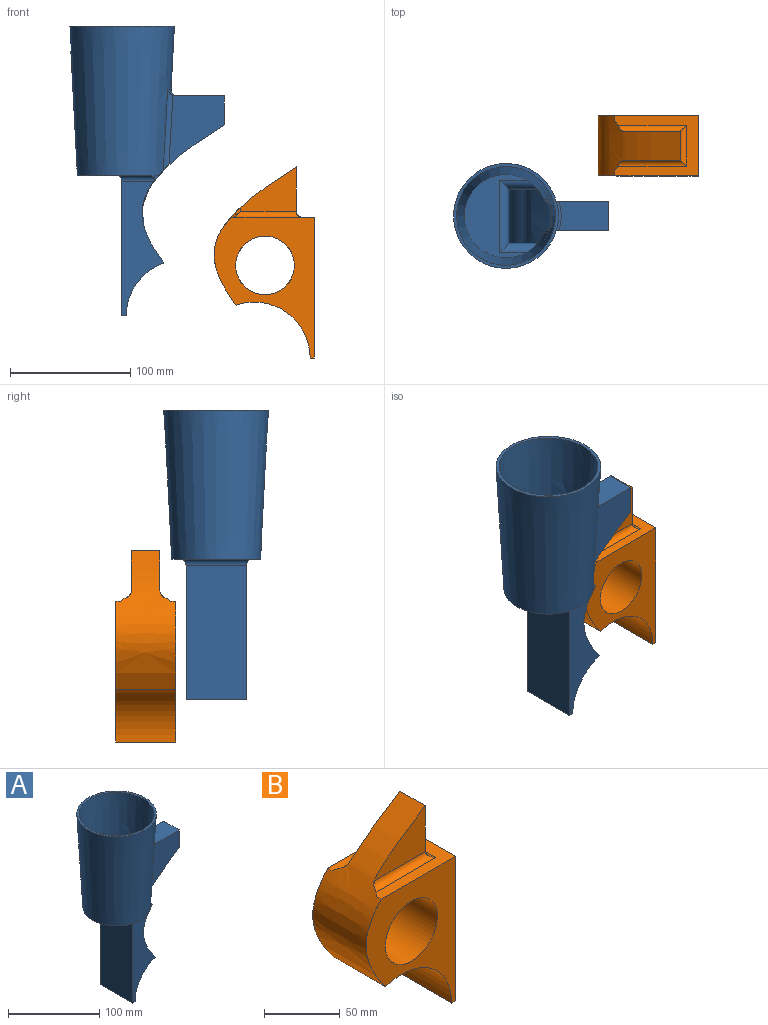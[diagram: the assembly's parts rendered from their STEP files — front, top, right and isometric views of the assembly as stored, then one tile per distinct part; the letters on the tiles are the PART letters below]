
ASSEMBLY  parts=2 mates=1
PART A: 40 faces, bbox 130.1x88.3x242.1 mm
  f0: plane 4.11x3.25mm, normal (0,0,1), area 6.4mm2, adj f2,f6,f22
  f1: plane 4.11x3.25mm, normal (0,0,1), area 6.4mm2, adj f2,f4,f22
  f2: cone r=37.09mm half-angle=3deg, axis (0,0,1), area 29261.2mm2, adj f0,f1,f4,f6,f11,f12,f13,f14
  f3: plane 113.11x35.98mm, normal (0,1,0), area 2016.9mm2, adj f10,f13,f15,f16,f22
  f4: plane 4.33x3.57mm, normal (0,1,0), area 6.8mm2, adj f1,f2,f22
  f5: plane 113.11x35.98mm, normal (0,-1,0), area 2016.9mm2, adj f10,f14,f15,f16,f22
  f6: plane 4.33x3.57mm, normal (0,-1,0), area 6.8mm2, adj f0,f2,f22
  f7: plane 58.25x46.77mm, normal (0,-1,0), area 1734.9mm2, adj f9,f12,f19,f20,f22
  f8: plane 58.25x46.77mm, normal (0,1,0), area 1734.9mm2, adj f9,f11,f19,f20,f22
  f9: plane 24.06x23.84mm, normal (1,0,0), area 573.7mm2, adj f7,f8,f19,f22
  f10: cylinder r=46.49mm len=50mm, axis (0,1,0), area 2880.8mm2, adj f3,f5,f15,f22
  f11: bspline ~111.12x10.85mm, area 369.3mm2, adj f2,f8,f20,f22
  f12: bspline ~111.12x10.85mm, area 369.3mm2, adj f2,f7,f20,f22
  f13: cylinder r=5mm len=32.05mm, axis (1,0,0), area 213.5mm2, adj f2,f3,f17,f21,f22
  f14: cylinder r=5mm len=32.05mm, axis (-1,0,0), area 213.5mm2, adj f2,f5,f17,f21,f22
  f15: plane 50x3.51mm, normal (0,0,-1), area 175.6mm2, adj f3,f5,f10,f16
  f16: plane 112x50mm, normal (-1,0,0), area 5600mm2, adj f3,f5,f15,f21
  f17: plane 74.18x58.91mm, normal (0,0,-1), area 2071.7mm2, adj f2,f13,f14,f21
  f18: plane 87.18x87.18mm, normal (0,0,1), area 666mm2, adj f2,f23
  f19: plane 40.75x23.84mm, normal (0,0,1), area 946.3mm2, adj f7,f8,f9,f20
  f20: torus R=45.82mm, axis (0,0,1), area 215.4mm2, adj f2,f7,f8,f11,f12,f19
  f21: cylinder r=5mm len=60mm, axis (0,1,0), area 432mm2, adj f13,f14,f16,f17
  f22: extruded ~114.98x68.32mm, area 5788.2mm2, adj f0,f1,f2,f3,f4,f5,f6,f7
  f23: cone r=34.6mm half-angle=3deg, axis (0,0,1), area 27057.6mm2, adj f18,f30,f31,f32,f33,f35,f37,f39
  f24: plane 100.02x28.4mm, normal (0,-1,0), area 1420.3mm2, adj f29,f32,f34,f39
  f25: plane 100.02x28.4mm, normal (0,1,0), area 1420.3mm2, adj f29,f33,f34,f39
  f26: plane 52.97x44.34mm, normal (0,1,0), area 1438.1mm2, adj f28,f31,f36,f37,f39
  f27: plane 52.97x44.34mm, normal (0,-1,0), area 1438.1mm2, adj f28,f30,f36,f37,f39
  f28: plane 20.2x18.84mm, normal (-1,0,0), area 380.6mm2, adj f26,f27,f36,f39
  f29: cylinder r=48.99mm len=45mm, axis (0,1,0), area 2034.9mm2, adj f24,f25,f34,f39
  f30: bspline ~111.25x13.12mm, area 522.6mm2, adj f23,f27,f37,f39
  f31: bspline ~111.25x13.12mm, area 522.6mm2, adj f23,f26,f37,f39
  f32: cylinder r=7.5mm len=30.62mm, axis (1,0,0), area 277.4mm2, adj f23,f24,f35,f38,f39
  f33: cylinder r=7.5mm len=30.62mm, axis (-1,0,0), area 277.4mm2, adj f23,f25,f35,f38,f39
  f34: plane 100.02x45mm, normal (1,0,0), area 4500.9mm2, adj f24,f25,f29,f38
  f35: plane 69.44x52.2mm, normal (0,0,1), area 1705.1mm2, adj f23,f32,f33,f38
  f36: plane 37.65x18.84mm, normal (0,0,-1), area 697mm2, adj f26,f27,f28,f37
  f37: torus R=45.82mm, axis (0,0,1), area 276.7mm2, adj f23,f26,f27,f30,f31,f36
  f38: cylinder r=7.5mm len=60mm, axis (0,1,0), area 618.5mm2, adj f32,f33,f34,f35
  f39: extruded ~115.19x68.35mm, area 5044.9mm2, adj f23,f24,f25,f26,f27,f28,f29,f30
PART B: 22 faces, bbox 84.4x50.1x163.9 mm
  f0: cylinder r=24.38mm len=50mm, axis (0,1,0), area 7659.3mm2, adj f16,f17
  f1: plane 117x50mm, normal (1,0,0), area 5850mm2, adj f3,f16,f17,f20
  f2: cylinder r=5mm len=33.84mm, axis (0,1,0), area 226.5mm2, adj f4,f5,f8,f20
  f3: plane 50x3.51mm, normal (0,0,-1), area 175.6mm2, adj f1,f15,f16,f17
  f4: cylinder r=5mm len=56.98mm, axis (-1,0,0), area 407.2mm2, adj f2,f7,f9,f12,f20
  f5: cylinder r=5mm len=56.98mm, axis (1,0,0), area 407.2mm2, adj f2,f6,f10,f11,f20
  f6: bspline ~69.55x8.5mm, area 20mm2, adj f5,f10,f11,f21
  f7: bspline ~69.55x8.5mm, area 20mm2, adj f4,f9,f12,f21
  f8: plane 36.94x23.84mm, normal (1,0,0), area 880.6mm2, adj f2,f9,f10,f21
  f9: plane 46.77x37.34mm, normal (0,1,0), area 974.8mm2, adj f4,f7,f8,f21
  f10: plane 46.77x37.34mm, normal (0,-1,0), area 974.8mm2, adj f5,f6,f8,f21
  f11: cone r=37.09mm half-angle=3deg, axis (0,0,1), area 12.6mm2, adj f5,f6,f20,f21
  f12: cone r=37.09mm half-angle=3deg, axis (0,0,1), area 12.6mm2, adj f4,f7,f20,f21
  f13: cylinder r=5mm len=0.63mm, axis (1,0,0), area 0.1mm2, adj f17,f19,f21
  f14: cylinder r=5mm len=0.63mm, axis (-1,0,0), area 0.1mm2, adj f16,f18,f21
  f15: cylinder r=46.49mm len=61.61mm, axis (0,1,0), area 4421.5mm2, adj f3,f16,f17,f21
  f16: plane 117.01x84.36mm, normal (0,-1,0), area 4278.1mm2, adj f0,f1,f3,f14,f15,f18,f20,f21
  f17: plane 117.01x84.36mm, normal (0,1,0), area 4278.1mm2, adj f0,f1,f3,f13,f15,f19,f20,f21
  f18: cone r=37.09mm half-angle=3deg, axis (0,0,1), area 0mm2, adj f14,f16,f21
  f19: cone r=37.09mm half-angle=3deg, axis (0,0,1), area 0mm2, adj f13,f17,f21
  f20: plane 69.35x50mm, normal (0,0,1), area 1449.6mm2, adj f1,f2,f4,f5,f11,f12,f16,f17
  f21: extruded ~114.98x68.32mm, area 5788.2mm2, adj f6,f7,f8,f9,f10,f11,f12,f13
PLACE A rot(axis=(0,-1,0),0deg) t=(22.1,-58.57,34.95)mm
PLACE B at identity fixed
MATE parallel A.f5 <-> B.f16  axis (0,-1,0) through (6.98,-83.57,78.91)mm
